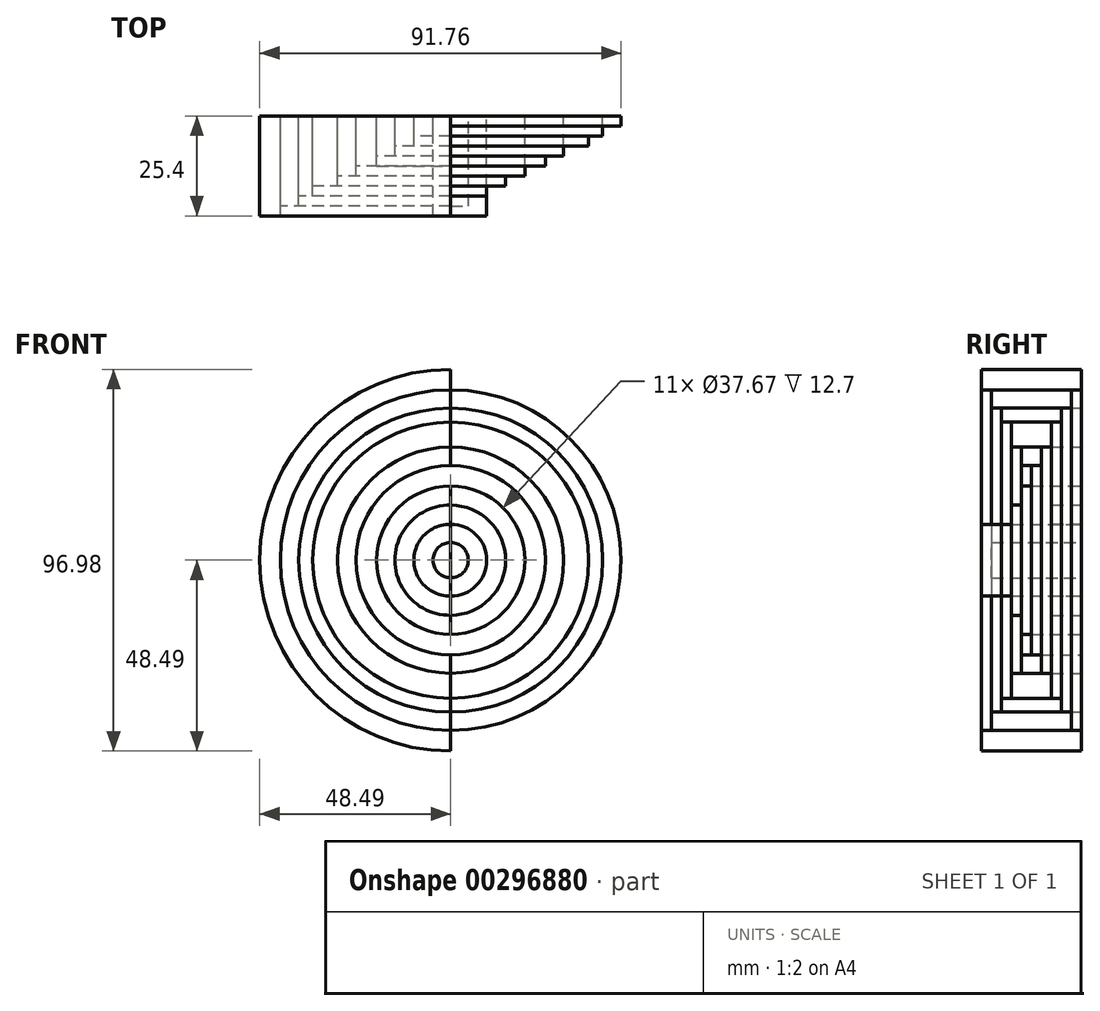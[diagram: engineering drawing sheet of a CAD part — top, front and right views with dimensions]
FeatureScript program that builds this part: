
annotation { "Feature Type Name" : "Feature", "Feature Type Description" : "" }
export const myFeature = defineFeature(function(context is Context, id is Id, definition is map)
    precondition{}
    {
        {
            var Q0;
            Q0=qCreatedBy(makeId("Front.planeOp"),FACE);
            var sketch = newSketch(context, id + "F0", { "sketchPlane" : qUnion([Q0])});
            skArc(sketch, "E0", {"start": v(0, 4.48) * mm, "mid": v(4.48, 0) * mm, "end": v(0, -4.48) * mm});
            skArc(sketch, "E1", {"start": v(0, 9.14) * mm, "mid": v(9.14, 0) * mm, "end": v(0, -9.14) * mm});
            skArc(sketch, "E2", {"start": v(0, 13.99) * mm, "mid": v(13.99, 0) * mm, "end": v(0, -13.99) * mm});
            skArc(sketch, "E3", {"start": v(0, 18.84) * mm, "mid": v(18.84, 0) * mm, "end": v(0, -18.84) * mm});
            skArc(sketch, "E4", {"start": v(0, 24.06) * mm, "mid": v(24.06, 0) * mm, "end": v(0, -24.06) * mm});
            skArc(sketch, "E5", {"start": v(0, 28.72) * mm, "mid": v(28.72, 0) * mm, "end": v(0, -28.72) * mm});
            skArc(sketch, "E6", {"start": v(0, 35.06) * mm, "mid": v(35.06, 0) * mm, "end": v(0, -35.06) * mm});
            skArc(sketch, "E7", {"start": v(0, 38.6) * mm, "mid": v(38.6, 0) * mm, "end": v(0, -38.6) * mm});
            skArc(sketch, "E8", {"start": v(0, 43.27) * mm, "mid": v(43.27, 0) * mm, "end": v(0, -43.27) * mm});
            skArc(sketch, "E9", {"start": v(0, 48.5) * mm, "mid": v(48.5, 0) * mm, "end": v(0, -48.5) * mm});
            skArc(sketch, "E10", {"start": v(0, 4.48) * mm, "mid": v(-4.48, 0) * mm, "end": v(0, -4.48) * mm});
            skArc(sketch, "E11", {"start": v(0, 9.14) * mm, "mid": v(-9.33, 0) * mm, "end": v(0, -9.14) * mm});
            skArc(sketch, "E12", {"start": v(0, 13.99) * mm, "mid": v(-14.18, 0) * mm, "end": v(0, -13.99) * mm});
            skArc(sketch, "E13", {"start": v(0, 18.84) * mm, "mid": v(-18.84, 0) * mm, "end": v(0, -18.84) * mm});
            skArc(sketch, "E14", {"start": v(0, 24.06) * mm, "mid": v(-24.06, 0) * mm, "end": v(0, -24.06) * mm});
            skArc(sketch, "E15", {"start": v(0, 28.72) * mm, "mid": v(-28.72, 0) * mm, "end": v(0, -28.72) * mm});
            skArc(sketch, "E16", {"start": v(0, 35.06) * mm, "mid": v(-35.06, 0) * mm, "end": v(0, -35.06) * mm});
            skArc(sketch, "E17", {"start": v(0, 38.6) * mm, "mid": v(-38.6, 0) * mm, "end": v(0, -38.6) * mm});
            skArc(sketch, "E18", {"start": v(0, 43.27) * mm, "mid": v(-43.27, 0) * mm, "end": v(0, -43.27) * mm});
            skArc(sketch, "E19", {"start": v(0, 48.5) * mm, "mid": v(-48.5, 0) * mm, "end": v(0, -48.5) * mm});
            skLineSegment(sketch, "E20", {"start": v(0, 48.5) * mm, "end": v(0, -48.5) * mm});
            skSolve(sketch);
        }
        {
            var Q0;
            {var subQ0=sQuery(id+"F0.wireOp",EDGE,"E8");Q0=makeQuery(id+"F0.imprint","IMPRINT",FACE,{"disambiguationData":[TD([[makeQuery(id+"F0.imprint","IMPRINT",EDGE,{"derivedFrom":subQ0}),1.0]])]});}
            extrude(context, id + "F1", {"entities" : qUnion([Q0]), "depth" : 2.54 * mm});
        }
        {
            var Q0;
            {var subQ0=sQuery(id+"F0.wireOp",EDGE,"E10");Q0=makeQuery(id+"F0.imprint","IMPRINT",FACE,{"disambiguationData":[TD([[makeQuery(id+"F0.imprint","IMPRINT",EDGE,{"derivedFrom":subQ0}),-1.0]])]});}
            var Q1;
            {var subQ0=sQuery(id+"F0.wireOp",EDGE,"E7");Q1=makeQuery(id+"F0.imprint","IMPRINT",FACE,{"disambiguationData":[TD([[makeQuery(id+"F0.imprint","IMPRINT",EDGE,{"derivedFrom":subQ0}),1.0]])]});}
            extrude(context, id + "F2", {"entities" : qUnion([Q0, Q1]), "depth" : 5.08 * mm});
        }
        {
            var Q0;
            {var subQ0=sQuery(id+"F0.wireOp",EDGE,"E11");Q0=makeQuery(id+"F0.imprint","IMPRINT",FACE,{"disambiguationData":[TD([[makeQuery(id+"F0.imprint","IMPRINT",EDGE,{"derivedFrom":subQ0}),-1.0]])]});}
            var Q1;
            {var subQ0=sQuery(id+"F0.wireOp",EDGE,"E6");Q1=makeQuery(id+"F0.imprint","IMPRINT",FACE,{"disambiguationData":[TD([[makeQuery(id+"F0.imprint","IMPRINT",EDGE,{"derivedFrom":subQ0}),1.0]])]});}
            extrude(context, id + "F3", {"entities" : qUnion([Q0, Q1]), "depth" : 7.62 * mm});
        }
        {
            var Q0;
            {var subQ0=sQuery(id+"F0.wireOp",EDGE,"E12");Q0=makeQuery(id+"F0.imprint","IMPRINT",FACE,{"disambiguationData":[TD([[makeQuery(id+"F0.imprint","IMPRINT",EDGE,{"derivedFrom":subQ0}),-1.0]])]});}
            var Q1;
            {var subQ0=sQuery(id+"F0.wireOp",EDGE,"E5");Q1=makeQuery(id+"F0.imprint","IMPRINT",FACE,{"disambiguationData":[TD([[makeQuery(id+"F0.imprint","IMPRINT",EDGE,{"derivedFrom":subQ0}),1.0]])]});}
            extrude(context, id + "F4", {"entities" : qUnion([Q0, Q1]), "depth" : 10.16 * mm});
        }
        {
            var Q0;
            {var subQ0=sQuery(id+"F0.wireOp",EDGE,"E13");Q0=makeQuery(id+"F0.imprint","IMPRINT",FACE,{"disambiguationData":[TD([[makeQuery(id+"F0.imprint","IMPRINT",EDGE,{"derivedFrom":subQ0}),-1.0]])]});}
            var Q1;
            {var subQ0=sQuery(id+"F0.wireOp",EDGE,"E4");Q1=makeQuery(id+"F0.imprint","IMPRINT",FACE,{"disambiguationData":[TD([[makeQuery(id+"F0.imprint","IMPRINT",EDGE,{"derivedFrom":subQ0}),1.0]])]});}
            extrude(context, id + "F5", {"entities" : qUnion([Q0, Q1]), "depth" : 12.7 * mm});
        }
        {
            var Q0;
            {var subQ0=sQuery(id+"F0.wireOp",EDGE,"E3");Q0=makeQuery(id+"F0.imprint","IMPRINT",FACE,{"disambiguationData":[TD([[makeQuery(id+"F0.imprint","IMPRINT",EDGE,{"derivedFrom":subQ0}),1.0]])]});}
            var Q1;
            {var subQ0=sQuery(id+"F0.wireOp",EDGE,"E14");Q1=makeQuery(id+"F0.imprint","IMPRINT",FACE,{"disambiguationData":[TD([[makeQuery(id+"F0.imprint","IMPRINT",EDGE,{"derivedFrom":subQ0}),-1.0]])]});}
            extrude(context, id + "F6", {"entities" : qUnion([Q0, Q1]), "depth" : 15.24 * mm});
        }
        {
            var Q0;
            {var subQ0=sQuery(id+"F0.wireOp",EDGE,"E15");Q0=makeQuery(id+"F0.imprint","IMPRINT",FACE,{"disambiguationData":[TD([[makeQuery(id+"F0.imprint","IMPRINT",EDGE,{"derivedFrom":subQ0}),-1.0]])]});}
            var Q1;
            {var subQ0=sQuery(id+"F0.wireOp",EDGE,"E2");Q1=makeQuery(id+"F0.imprint","IMPRINT",FACE,{"disambiguationData":[TD([[makeQuery(id+"F0.imprint","IMPRINT",EDGE,{"derivedFrom":subQ0}),1.0]])]});}
            extrude(context, id + "F7", {"entities" : qUnion([Q0, Q1]), "depth" : 17.78 * mm});
        }
        {
            var Q0;
            {var subQ0=sQuery(id+"F0.wireOp",EDGE,"E1");Q0=makeQuery(id+"F0.imprint","IMPRINT",FACE,{"disambiguationData":[TD([[makeQuery(id+"F0.imprint","IMPRINT",EDGE,{"derivedFrom":subQ0}),1.0]])]});}
            var Q1;
            {var subQ0=sQuery(id+"F0.wireOp",EDGE,"E16");Q1=makeQuery(id+"F0.imprint","IMPRINT",FACE,{"disambiguationData":[TD([[makeQuery(id+"F0.imprint","IMPRINT",EDGE,{"derivedFrom":subQ0}),-1.0]])]});}
            extrude(context, id + "F8", {"entities" : qUnion([Q0, Q1]), "depth" : 20.32 * mm});
        }
        {
            var Q0;
            {var subQ0=sQuery(id+"F0.wireOp",EDGE,"E17");Q0=makeQuery(id+"F0.imprint","IMPRINT",FACE,{"disambiguationData":[TD([[makeQuery(id+"F0.imprint","IMPRINT",EDGE,{"derivedFrom":subQ0}),-1.0]])]});}
            var Q1;
            {var subQ0=sQuery(id+"F0.wireOp",EDGE,"E0");Q1=makeQuery(id+"F0.imprint","IMPRINT",FACE,{"disambiguationData":[TD([[makeQuery(id+"F0.imprint","IMPRINT",EDGE,{"derivedFrom":subQ0}),1.0]])]});}
            extrude(context, id + "F9", {"entities" : qUnion([Q0, Q1]), "depth" : 22.86 * mm});
        }
        {
            var Q0;
            {var subQ0=sQuery(id+"F0.wireOp",EDGE,"E18");Q0=makeQuery(id+"F0.imprint","IMPRINT",FACE,{"disambiguationData":[TD([[makeQuery(id+"F0.imprint","IMPRINT",EDGE,{"derivedFrom":subQ0}),-1.0]])]});}
            var Q1;
            {var subQ0=sQuery(id+"F0.wireOp",EDGE,"E0");Q1=makeQuery(id+"F0.imprint","IMPRINT",FACE,{"disambiguationData":[TD([[makeQuery(id+"F0.imprint","IMPRINT",EDGE,{"derivedFrom":subQ0}),-1.0]])]});}
            extrude(context, id + "F10", {"entities" : qUnion([Q0, Q1]), "depth" : 25.4 * mm});
        }
        {
            var Q0;
            {var subQ0=sQuery(id+"F0.wireOp",EDGE,"E10");Q0=makeQuery(id+"F0.imprint","IMPRINT",FACE,{"disambiguationData":[TD([[makeQuery(id+"F0.imprint","IMPRINT",EDGE,{"derivedFrom":subQ0}),1.0]])]});}
            extrude(context, id + "F11", {"entities" : qUnion([Q0]), "depth" : 25.4 * mm});
        }
    });
